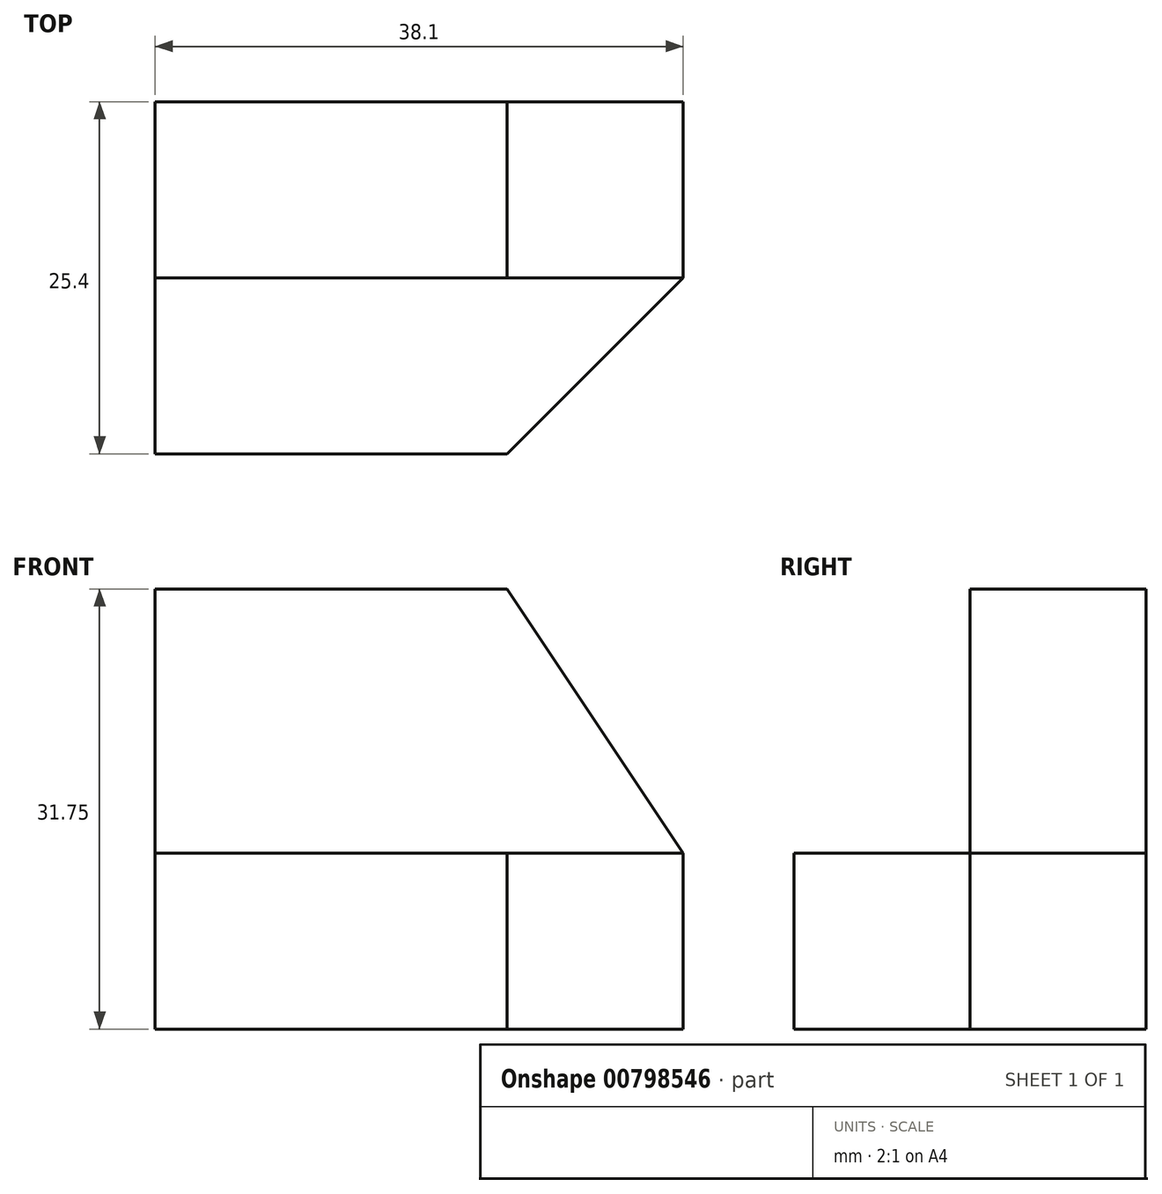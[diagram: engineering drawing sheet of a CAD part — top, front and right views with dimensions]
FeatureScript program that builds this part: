
annotation { "Feature Type Name" : "Feature", "Feature Type Description" : "" }
export const myFeature = defineFeature(function(context is Context, id is Id, definition is map)
    precondition{}
    {
        {
            var Q0;
            Q0=qCreatedBy(makeId("Front.planeOp"),FACE);
            var sketch = newSketch(context, id + "F0", { "sketchPlane" : qUnion([Q0])});
            skLineSegment(sketch, "E0", {"start": v(0, 0) * mm, "end": v(38.1, 0) * mm});
            skLineSegment(sketch, "E1", {"start": v(0, 0) * mm, "end": v(0, 31.75) * mm});
            skLineSegment(sketch, "E2", {"start": v(0, 31.75) * mm, "end": v(38.1, 31.75) * mm});
            skLineSegment(sketch, "E3", {"start": v(38.1, 31.75) * mm, "end": v(38.1, 0) * mm});
            skSolve(sketch);
        }
        {
            var Q0;
            Q0=makeQuery(id+"F0.imprint","IMPRINT",FACE,{"disambiguationData":[TD([[makeQuery(id+"F0.imprint","IMPRINT",EDGE,{"derivedFrom":sQuery(id+"F0.wireOp",EDGE,"E0")}),1.0]])]});
            extrude(context, id + "F1", {"entities" : qUnion([Q0]), "depth" : 25.4 * mm, "offsetDistance" : 25.4 * mm});
        }
        {
            var Q0;
            Q0=makeQuery(id+"F1.opExtrude","SWEPT_FACE",FACE,{"disambiguationData":[OSD([sQuery(id+"F0.wireOp",EDGE,"E2")])]});
            var sketch = newSketch(context, id + "F2", { "sketchPlane" : qUnion([Q0])});
            skLineSegment(sketch, "E4", {"start": v(0, -25.4) * mm, "end": v(0, -12.7) * mm});
            skLineSegment(sketch, "E5", {"start": v(0, -12.7) * mm, "end": v(38.1, -12.7) * mm});
            skSolve(sketch);
        }
        {
            var Q0;
            Q0=makeQuery(id+"F2.imprint","IMPRINT",FACE,{"disambiguationData":[TD([[makeQuery(id+"F2.imprint","IMPRINT",EDGE,{"derivedFrom":sQuery(id+"F2.wireOp",EDGE,"E4")}),-1.0]])]});
            extrude(context, id + "F3", {"entities" : qUnion([Q0]), "operationType" : NewBodyOperationType.REMOVE, "oppositeDirection" : true, "depth" : 19.05 * mm, "offsetDistance" : 25.4 * mm});
        }
        {
            var Q0;
            Q0=makeQuery(id+"F3.boolean.opBoolean","COPY",FACE,{"derivedFrom":makeQuery(id+"F3.opExtrude","SWEPT_FACE",FACE,{"disambiguationData":[OSD([sQuery(id+"F2.wireOp",EDGE,"E5")])]})});
            var sketch = newSketch(context, id + "F4", { "sketchPlane" : qUnion([Q0])});
            skLineSegment(sketch, "E6", {"start": v(0, 31.75) * mm, "end": v(25.4, 31.75) * mm});
            skLineSegment(sketch, "E7", {"start": v(25.4, 31.75) * mm, "end": v(38.1, 12.7) * mm});
            skSolve(sketch);
        }
        {
            var Q0;
            {var subQ0=sQuery(id+"F4.wireOp",EDGE,"E7");Q0=makeQuery(id+"F4.imprint","IMPRINT",FACE,{"disambiguationData":[TD([[makeQuery(id+"F4.imprint","IMPRINT",EDGE,{"derivedFrom":subQ0}),1.0]])]});}
            extrude(context, id + "F5", {"entities" : qUnion([Q0]), "operationType" : NewBodyOperationType.REMOVE, "endBound" : BoundingType.THROUGH_ALL, "oppositeDirection" : true, "depth" : 25.4 * mm, "offsetDistance" : 25.4 * mm});
        }
        {
            var Q0;
            Q0=makeQuery(id+"F3.boolean.opBoolean","COPY",FACE,{"derivedFrom":makeQuery(id+"F3.opExtrude","CAP_FACE",FACE,{"disambiguationData":[OSD([sQuery(id+"F0.wireOp",EDGE,"E2"),sQuery(id+"F0.wireOp",EDGE,"E3"),sQuery(id+"F2.wireOp",EDGE,"E4"),sQuery(id+"F2.wireOp",EDGE,"E5")])],"isStart":false})});
            var sketch = newSketch(context, id + "F6", { "sketchPlane" : qUnion([Q0])});
            skLineSegment(sketch, "E8", {"start": v(0, -25.4) * mm, "end": v(25.4, -25.4) * mm});
            skLineSegment(sketch, "E9", {"start": v(25.4, -25.4) * mm, "end": v(38.1, -12.7) * mm});
            skSolve(sketch);
        }
        {
            var Q0;
            {var subQ0=sQuery(id+"F6.wireOp",EDGE,"E9");Q0=makeQuery(id+"F6.imprint","IMPRINT",FACE,{"disambiguationData":[TD([[makeQuery(id+"F6.imprint","IMPRINT",EDGE,{"derivedFrom":subQ0}),-1.0]])]});}
            extrude(context, id + "F7", {"entities" : qUnion([Q0]), "operationType" : NewBodyOperationType.REMOVE, "endBound" : BoundingType.THROUGH_ALL, "oppositeDirection" : true, "depth" : 25.4 * mm, "offsetDistance" : 25.4 * mm});
        }
    });
